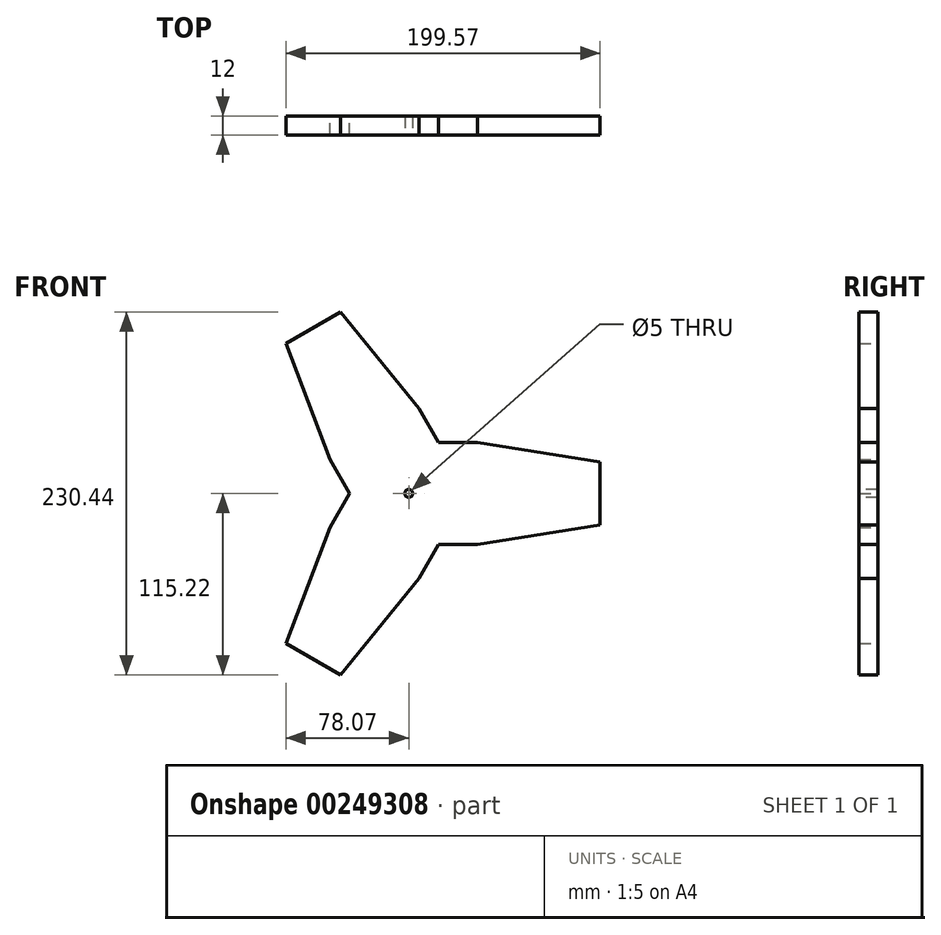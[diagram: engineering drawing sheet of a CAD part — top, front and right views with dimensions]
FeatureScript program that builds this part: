
annotation { "Feature Type Name" : "Feature", "Feature Type Description" : "" }
export const myFeature = defineFeature(function(context is Context, id is Id, definition is map)
    precondition{}
    {
        {
            var Q0;
            Q0=qCreatedBy(makeId("Front.planeOp"),FACE);
            var sketch = newSketch(context, id + "F0", { "sketchPlane" : qUnion([Q0])});
            skLineSegment(sketch, "E0", {"start": v(121.5, -20) * mm, "end": v(121.5, 20) * mm});
            skLineSegment(sketch, "E1", {"start": v(121.5, 20) * mm, "end": v(43.52, 32.5) * mm});
            skLineSegment(sketch, "E2", {"start": v(43.52, 32.5) * mm, "end": v(25, 32.5) * mm});
            skLineSegment(sketch, "E3", {"start": v(25, 32.5) * mm, "end": v(25, -32.5) * mm, "construction": true});
            skLineSegment(sketch, "E4", {"start": v(43.52, -32.5) * mm, "end": v(121.5, -20) * mm});
            skPoint(sketch, "E5.center", {"position": v(0, 0) * mm});
            skLineSegment(sketch, "E6", {"start": v(43.52, -32.5) * mm, "end": v(25, -32.5) * mm});
            skLineSegment(sketch, "E7", {"start": v(25, 32.5) * mm, "end": v(0, 32.5) * mm});
            skLineSegment(sketch, "E8", {"start": v(25, -32.5) * mm, "end": v(0, -32.5) * mm});
            skLineSegment(sketch, "E9.1.0", {"start": v(-43.43, 115.22) * mm, "end": v(-78.07, 95.22) * mm});
            skLineSegment(sketch, "E9.1.1", {"start": v(6.38, 53.94) * mm, "end": v(-43.43, 115.22) * mm});
            skLineSegment(sketch, "E9.1.2", {"start": v(-40.65, 5.4) * mm, "end": v(-28.15, -16.25) * mm});
            skLineSegment(sketch, "E9.1.3", {"start": v(-49.9, 21.44) * mm, "end": v(-40.65, 5.4) * mm});
            skLineSegment(sketch, "E9.1.4", {"start": v(-40.65, 5.4) * mm, "end": v(15.65, 37.9) * mm, "construction": true});
            skLineSegment(sketch, "E9.1.5", {"start": v(-78.07, 95.22) * mm, "end": v(-49.9, 21.44) * mm});
            skLineSegment(sketch, "E9.1.6", {"start": v(15.65, 37.9) * mm, "end": v(28.15, 16.25) * mm});
            skLineSegment(sketch, "E9.1.7", {"start": v(6.38, 53.94) * mm, "end": v(15.65, 37.9) * mm});
            skLineSegment(sketch, "E9.2.0", {"start": v(-78.07, -95.22) * mm, "end": v(-43.43, -115.22) * mm});
            skLineSegment(sketch, "E9.2.1", {"start": v(-49.9, -21.44) * mm, "end": v(-78.07, -95.22) * mm});
            skLineSegment(sketch, "E9.2.2", {"start": v(15.65, -37.9) * mm, "end": v(28.15, -16.25) * mm});
            skLineSegment(sketch, "E9.2.3", {"start": v(6.38, -53.94) * mm, "end": v(15.65, -37.9) * mm});
            skLineSegment(sketch, "E9.2.4", {"start": v(15.65, -37.9) * mm, "end": v(-40.65, -5.4) * mm, "construction": true});
            skLineSegment(sketch, "E9.2.5", {"start": v(-43.43, -115.22) * mm, "end": v(6.38, -53.94) * mm});
            skLineSegment(sketch, "E9.2.6", {"start": v(-40.65, -5.4) * mm, "end": v(-28.15, 16.25) * mm});
            skLineSegment(sketch, "E9.2.7", {"start": v(-49.9, -21.44) * mm, "end": v(-40.65, -5.4) * mm});
            skPoint(sketch, "E10", {"position": v(18.76, 32.5) * mm});
            skLineSegment(sketch, "E11", {"start": v(0, 0) * mm, "end": v(18.76, 32.5) * mm});
            skSolve(sketch);
        }
        {
            var Q0;
            Q0=makeQuery(id+"F0.imprint","IMPRINT",FACE,{"disambiguationData":[TD([[makeQuery(id+"F0.imprint","IMPRINT",EDGE,{"derivedFrom":sQuery(id+"F0.wireOp",EDGE,"E5.1.0")}),1.0]])]});
            var Q1;
            Q1=makeQuery(id+"F0.imprint","IMPRINT",FACE,{"disambiguationData":[TD([[makeQuery(id+"F0.imprint","IMPRINT",EDGE,{"derivedFrom":sQuery(id+"F0.wireOp",EDGE,"E0")}),1.0]])]});
            var Q2;
            Q2=makeQuery(id+"F0.imprint","IMPRINT",FACE,{"disambiguationData":[TD([[makeQuery(id+"F0.imprint","IMPRINT",EDGE,{"derivedFrom":sQuery(id+"F0.wireOp",EDGE,"E5.2.0")}),1.0]])]});
            extrude(context, id + "F1", {"entities" : qUnion([Q0, Q1, Q2]), "depth" : 12 * mm, "offsetDistance" : 25 * mm, "symmetric" : true});
        }
        {
            var Q0;
            Q0=makeQuery(id+"F1.opExtrude","CAP_FACE",FACE,{"disambiguationData":[OSD([sQuery(id+"F0.wireOp",EDGE,"E0"),sQuery(id+"F0.wireOp",EDGE,"E1"),sQuery(id+"F0.wireOp",EDGE,"E2"),sQuery(id+"F0.wireOp",EDGE,"8ubO5jFa-QZ4h-9gPm-ABJ2-z6dTXF6rIyxZ"),sQuery(id+"F0.wireOp",EDGE,"E4"),sQuery(id+"F0.wireOp",EDGE,"196ab397-e85d-45d6-b90e-64f27e1279f8.1.0"),sQuery(id+"F0.wireOp",EDGE,"196ab397-e85d-45d6-b90e-64f27e1279f8.1.1"),sQuery(id+"F0.wireOp",EDGE,"196ab397-e85d-45d6-b90e-64f27e1279f8.1.2"),sQuery(id+"F0.wireOp",EDGE,"196ab397-e85d-45d6-b90e-64f27e1279f8.1.3"),sQuery(id+"F0.wireOp",EDGE,"196ab397-e85d-45d6-b90e-64f27e1279f8.1.5"),sQuery(id+"F0.wireOp",EDGE,"196ab397-e85d-45d6-b90e-64f27e1279f8.2.0"),sQuery(id+"F0.wireOp",EDGE,"196ab397-e85d-45d6-b90e-64f27e1279f8.2.1"),sQuery(id+"F0.wireOp",EDGE,"196ab397-e85d-45d6-b90e-64f27e1279f8.2.2"),sQuery(id+"F0.wireOp",EDGE,"196ab397-e85d-45d6-b90e-64f27e1279f8.2.3"),sQuery(id+"F0.wireOp",EDGE,"196ab397-e85d-45d6-b90e-64f27e1279f8.2.5"),sQuery(id+"F0.wireOp",EDGE,"dfdRpkrF-JzXj-eirR-y30L-qTKLwPED3wTK")])],"isStart":false});
            var sketch = newSketch(context, id + "F2", { "sketchPlane" : qUnion([Q0])});
            skCircle(sketch, "E12", {"center": v(0, 0) * mm, "radius": 2.5 * mm});
            skSolve(sketch);
        }
        {
            var Q0;
            Q0=qSketchRegion(id+"F2",true);
            extrude(context, id + "F3", {"entities" : qUnion([Q0]), "operationType" : NewBodyOperationType.REMOVE, "endBound" : BoundingType.THROUGH_ALL, "oppositeDirection" : true, "depth" : 25 * mm, "offsetDistance" : 25 * mm});
        }
    });
